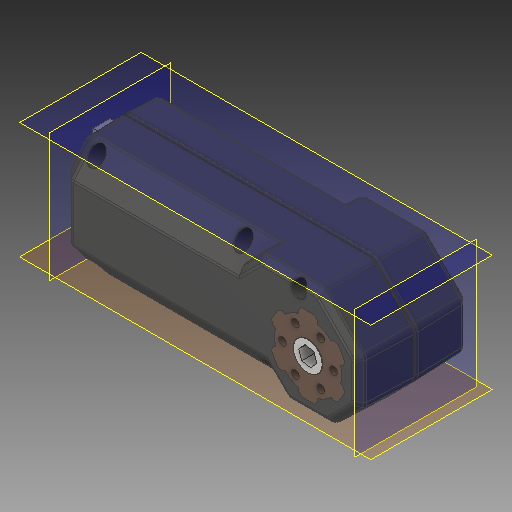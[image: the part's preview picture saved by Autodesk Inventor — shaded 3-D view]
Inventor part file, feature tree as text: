
AUTODESK INVENTOR PART (.ipt)
format: ipt  version: 2019 (Build 230136000, 136)  size: 7,768,064 bytes
history: native  units: in
note: dims shown in document units (in); Inventor stores cm internally (conversion verified against a paired STEP export)
features: other x10, plane x4
ambient origin geometry x8: Origin, YZ Plane, XZ Plane, XY Plane, X Axis, Y Axis, Z Axis, Center Point
bodies: Solid1 (feature_tree), Solid2 (feature_tree), Solid3 (feature_tree), Solid4 (feature_tree), Solid5 (feature_tree), Solid6 (feature_tree), Solid7 (feature_tree), Solid8 (feature_tree)
feature tree (14):
  plane  "Work Plane1"
  plane  "Work Plane2"
  plane  "Work Plane3"
  plane  "Work Plane4"
  parser-record x1  (decoder bookkeeping rows leaked as tree rows — omitted from the tree; the rows remain in map.json)
  other  "NONE:1"
  other  "NONE:2"
  other  "NONE:3"
  other  "NONE:4"
  other  "NONE:5"
  other  "NONE:6"
  other  "NONE:7"
  other  "Composite1"
  other  "Srf1"
